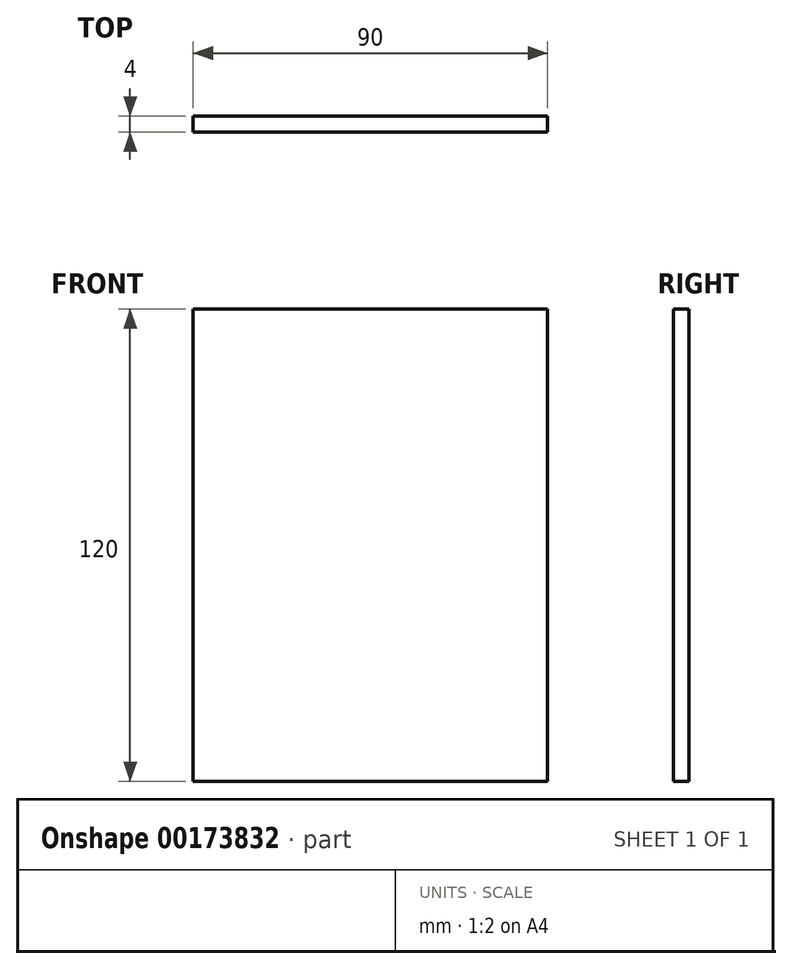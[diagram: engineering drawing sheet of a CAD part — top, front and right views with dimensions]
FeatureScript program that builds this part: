
annotation { "Feature Type Name" : "Feature", "Feature Type Description" : "" }
export const myFeature = defineFeature(function(context is Context, id is Id, definition is map)
    precondition{}
    {
        {
            var Q0;
            Q0=qCreatedBy(makeId("Front.planeOp"),FACE);
            var sketch = newSketch(context, id + "F0", { "sketchPlane" : qUnion([Q0])});
            skLineSegment(sketch, "E0.bottom", {"start": v(0, 0) * mm, "end": v(90, 0) * mm});
            skLineSegment(sketch, "E0.top", {"start": v(0, 120) * mm, "end": v(90, 120) * mm});
            skLineSegment(sketch, "E0.left", {"start": v(0, 0) * mm, "end": v(0, 120) * mm});
            skLineSegment(sketch, "E0.right", {"start": v(90, 0) * mm, "end": v(90, 120) * mm});
            skSolve(sketch);
        }
        {
            var Q0;
            Q0 = qSketchRegion(id + "F0", true);
            extrude(context, id + "F1", {"entities" : qUnion([Q0]), "depth" : 4 * mm});
        }
    });
